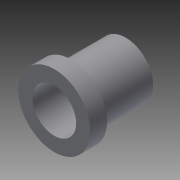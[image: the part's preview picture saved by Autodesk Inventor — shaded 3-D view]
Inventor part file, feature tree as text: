
AUTODESK INVENTOR PART (.ipt)
format: ipt  version: 2014 (Build 180170000, 170)  size: 106,496 bytes
history: native  units: in
note: dims shown in document units (in); Inventor stores cm internally (conversion verified against a paired STEP export)
features: sketch x3, extrude x3, plane x2, reference x1
ambient origin geometry x8: Origin, YZ Plane, XZ Plane, XY Plane, X Axis, Y Axis, Z Axis, Center Point
bodies: Solid1 (feature_tree)
feature tree (9):
  plane  "Work Plane1"
  sketch  "Sketch1"  dims[d0=0.01in d1=0.52in]
  plane  "Work Plane2"
  extrude  "Extrusion1"  Depth=0.52in
  extrude  "Extrusion2"  Depth=0.1in
  extrude  "Extrusion4"  Depth=0.1in
  reference  "Reference1"
  sketch  "Sketch2"  dims[d2=1.0in d3=0.0in d4=0.1in]
  sketch  "Sketch4"  dims[d5=0.2in d6=0.0in d9=0.1in d10=0.1in d11=0.0in]
